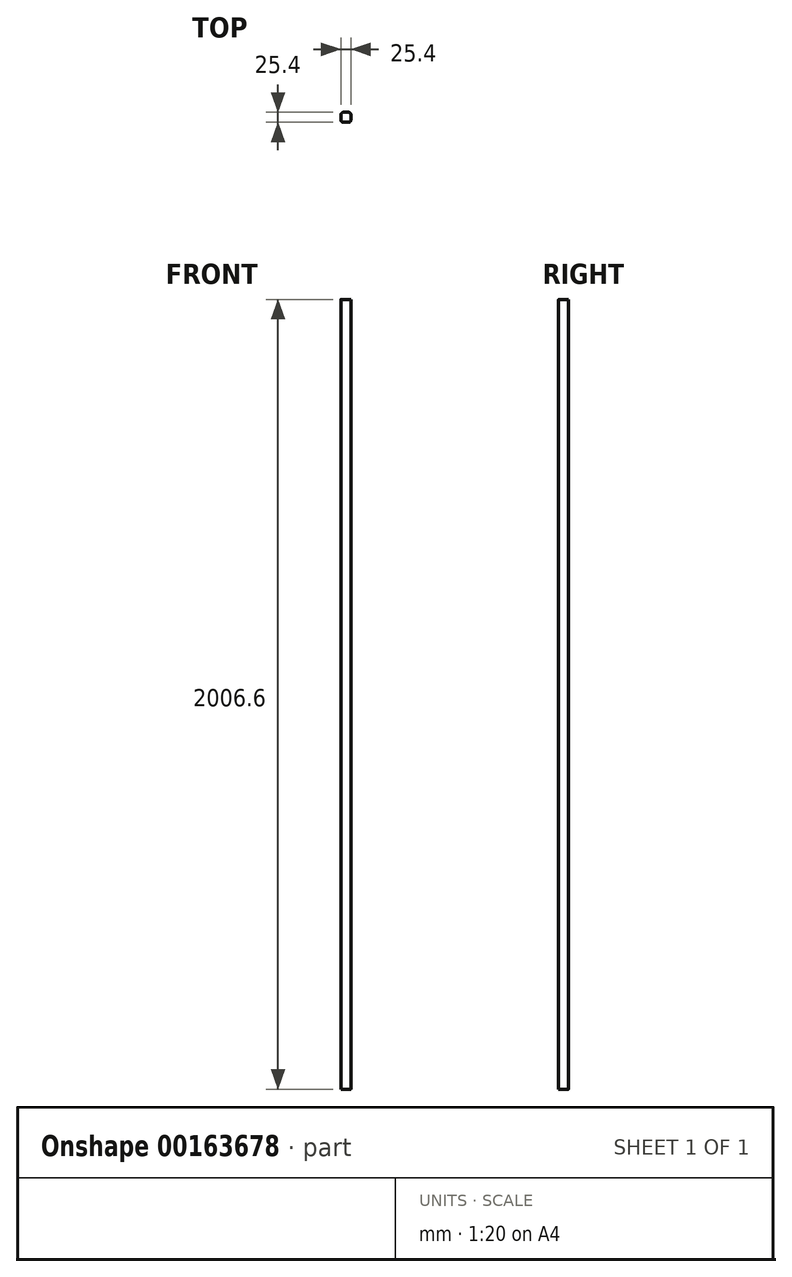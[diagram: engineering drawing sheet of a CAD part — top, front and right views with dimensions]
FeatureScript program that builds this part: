
annotation { "Feature Type Name" : "Feature", "Feature Type Description" : "" }
export const myFeature = defineFeature(function(context is Context, id is Id, definition is map)
    precondition{}
    {
        {
            var Q0;
            Q0=qCreatedBy(makeId("Top.planeOp"),FACE);
            var sketch = newSketch(context, id + "F0", { "sketchPlane" : qUnion([Q0])});
            skLineSegment(sketch, "E0.bottom", {"start": v(6.35, 12.7) * mm, "end": v(-6.35, 12.7) * mm});
            skLineSegment(sketch, "E0.top", {"start": v(6.35, -12.7) * mm, "end": v(-6.35, -12.7) * mm});
            skLineSegment(sketch, "E0.left", {"start": v(12.7, 6.35) * mm, "end": v(12.7, -6.35) * mm});
            skLineSegment(sketch, "E0.right", {"start": v(-12.7, 6.35) * mm, "end": v(-12.7, -6.35) * mm});
            skPoint(sketch, "E0.middle", {"position": v(0, 0) * mm});
            skPoint(sketch, "E1.visualSharp", {"position": v(-12.7, 12.7) * mm});
            skArc(sketch, "E1.filletArc", {"start": v(-6.35, 12.7) * mm, "mid": v(-10.84, 10.84) * mm, "end": v(-12.7, 6.35) * mm});
            skPoint(sketch, "E2.visualSharp", {"position": v(-12.7, -12.7) * mm});
            skArc(sketch, "E2.filletArc", {"start": v(-12.7, -6.35) * mm, "mid": v(-10.84, -10.84) * mm, "end": v(-6.35, -12.7) * mm});
            skPoint(sketch, "E3.visualSharp", {"position": v(12.7, -12.7) * mm});
            skArc(sketch, "E3.filletArc", {"start": v(6.35, -12.7) * mm, "mid": v(10.84, -10.84) * mm, "end": v(12.7, -6.35) * mm});
            skPoint(sketch, "E4.visualSharp", {"position": v(12.7, 12.7) * mm});
            skArc(sketch, "E4.filletArc", {"start": v(12.7, 6.35) * mm, "mid": v(10.84, 10.84) * mm, "end": v(6.35, 12.7) * mm});
            skSolve(sketch);
        }
        {
            var Q0;
            Q0=qSketchRegion(id+"F0",true);
            extrude(context, id + "F1", {"entities" : qUnion([Q0]), "depth" : 2006.6 * mm, "offsetDistance" : 25.4 * mm});
        }
    });
